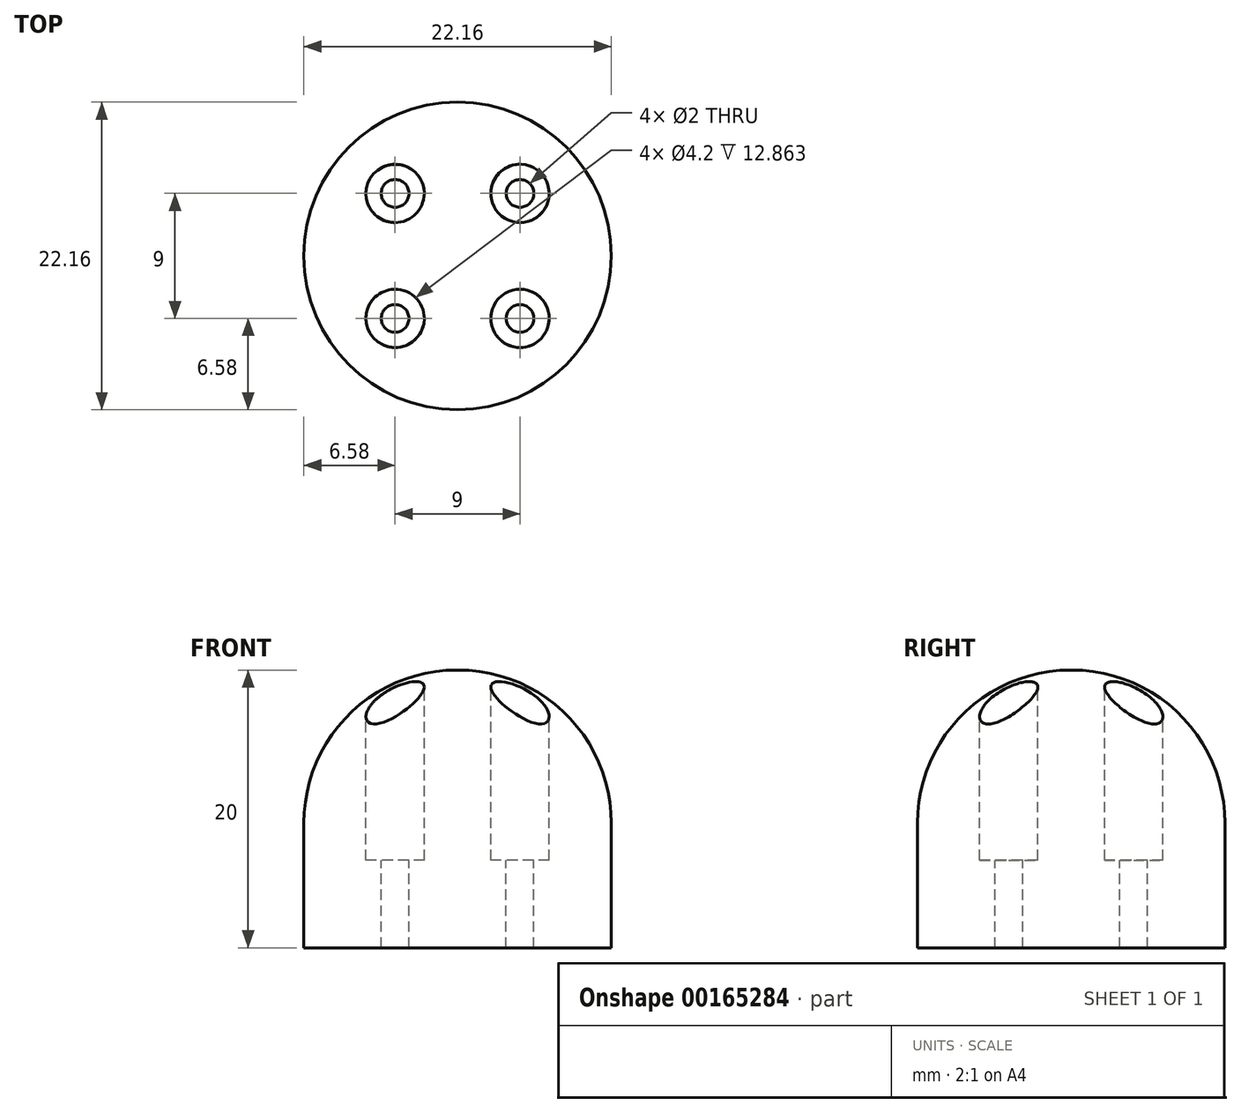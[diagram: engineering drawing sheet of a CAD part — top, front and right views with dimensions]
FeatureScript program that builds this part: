
annotation { "Feature Type Name" : "Feature", "Feature Type Description" : "" }
export const myFeature = defineFeature(function(context is Context, id is Id, definition is map)
    precondition{}
    {
        {
            var Q0;
            Q0=qCreatedBy(makeId("Top.planeOp"),FACE);
            var sketch = newSketch(context, id + "F0", { "sketchPlane" : qUnion([Q0])});
            skCircle(sketch, "E0", {"center": v(0, 0) * mm, "radius": 11.07 * mm});
            skSolve(sketch);
        }
        {
            var Q0;
            Q0=qSketchRegion(id+"F0",true);
            extrude(context, id + "F1", {"entities" : qUnion([Q0]), "depth" : 20 * mm});
        }
        {
            var Q0;
            Q0=makeQuery(id+"F1.opExtrude","CAP_FACE",FACE,{"disambiguationData":[OSD([sQuery(id+"F0.wireOp",EDGE,"E0")])],"isStart":false});
            var sketch = newSketch(context, id + "F2", { "sketchPlane" : qUnion([Q0])});
            skLineSegment(sketch, "E1.bottom", {"start": v(4.5, 4.5) * mm, "end": v(-4.5, 4.5) * mm});
            skLineSegment(sketch, "E1.top", {"start": v(4.5, -4.5) * mm, "end": v(-4.5, -4.5) * mm});
            skLineSegment(sketch, "E1.left", {"start": v(4.5, 4.5) * mm, "end": v(4.5, -4.5) * mm});
            skLineSegment(sketch, "E1.right", {"start": v(-4.5, 4.5) * mm, "end": v(-4.5, -4.5) * mm});
            skPoint(sketch, "E1.middle", {"position": v(0, 0) * mm});
            skCircle(sketch, "E2", {"center": v(-4.5, 4.5) * mm, "radius": 1 * mm, "construction": true});
            skCircle(sketch, "E3", {"center": v(4.5, 4.5) * mm, "radius": 1 * mm, "construction": true});
            skCircle(sketch, "E4", {"center": v(4.5, -4.5) * mm, "radius": 1 * mm, "construction": true});
            skCircle(sketch, "E5", {"center": v(-4.5, -4.5) * mm, "radius": 1 * mm, "construction": true});
            skCircle(sketch, "E6", {"center": v(-4.5, -4.5) * mm, "radius": 1 * mm});
            skCircle(sketch, "E7", {"center": v(-4.5, 4.5) * mm, "radius": 1 * mm});
            skCircle(sketch, "E8", {"center": v(4.5, 4.5) * mm, "radius": 1 * mm});
            skCircle(sketch, "E9", {"center": v(4.5, -4.5) * mm, "radius": 1 * mm});
            skSolve(sketch);
        }
        {
            var Q0;
            {var subQ0=sQuery(id+"F2.wireOp",EDGE,"E1.left");var subQ1=sQuery(id+"F2.wireOp",EDGE,"E1.bottom");var subQ2=makeQuery(id+"F2.imprint","INTERSECT",VERTEX,{"derivedFrom":[subQ1,subQ0]});Q0=makeQuery(id+"F2.imprint","IMPRINT",FACE,{"disambiguationData":[TD([[makeQuery(id+"F2.imprint","IMPRINT",EDGE,{"disambiguationData":[TD([[subQ2,-1.0]])],"derivedFrom":subQ1}),1.0]])]});}
            var Q1;
            {var subQ0=sQuery(id+"F2.wireOp",EDGE,"E1.right");var subQ1=sQuery(id+"F2.wireOp",EDGE,"E1.bottom");var subQ2=makeQuery(id+"F2.imprint","INTERSECT",VERTEX,{"derivedFrom":[subQ1,subQ0]});Q1=makeQuery(id+"F2.imprint","IMPRINT",FACE,{"disambiguationData":[TD([[makeQuery(id+"F2.imprint","IMPRINT",EDGE,{"disambiguationData":[TD([[subQ2,1.0]])],"derivedFrom":subQ1}),-1.0]])]});}
            var Q2;
            {var subQ0=sQuery(id+"F2.wireOp",EDGE,"E1.right");var subQ1=sQuery(id+"F2.wireOp",EDGE,"E1.bottom");var subQ2=makeQuery(id+"F2.imprint","INTERSECT",VERTEX,{"derivedFrom":[subQ1,subQ0]});Q2=makeQuery(id+"F2.imprint","IMPRINT",FACE,{"disambiguationData":[TD([[makeQuery(id+"F2.imprint","IMPRINT",EDGE,{"disambiguationData":[TD([[subQ2,1.0]])],"derivedFrom":subQ1}),1.0]])]});}
            var Q3;
            {var subQ0=sQuery(id+"F2.wireOp",EDGE,"E1.left");var subQ1=sQuery(id+"F2.wireOp",EDGE,"E1.top");var subQ2=makeQuery(id+"F2.imprint","INTERSECT",VERTEX,{"derivedFrom":[subQ1,subQ0]});Q3=makeQuery(id+"F2.imprint","IMPRINT",FACE,{"disambiguationData":[TD([[makeQuery(id+"F2.imprint","IMPRINT",EDGE,{"disambiguationData":[TD([[subQ2,-1.0]])],"derivedFrom":subQ1}),-1.0]])]});}
            var Q4;
            {var subQ0=sQuery(id+"F2.wireOp",EDGE,"E1.left");var subQ1=sQuery(id+"F2.wireOp",EDGE,"E1.top");var subQ2=makeQuery(id+"F2.imprint","INTERSECT",VERTEX,{"derivedFrom":[subQ1,subQ0]});Q4=makeQuery(id+"F2.imprint","IMPRINT",FACE,{"disambiguationData":[TD([[makeQuery(id+"F2.imprint","IMPRINT",EDGE,{"disambiguationData":[TD([[subQ2,-1.0]])],"derivedFrom":subQ1}),1.0]])]});}
            var Q5;
            {var subQ0=sQuery(id+"F2.wireOp",EDGE,"E1.right");var subQ1=sQuery(id+"F2.wireOp",EDGE,"E1.top");var subQ2=makeQuery(id+"F2.imprint","INTERSECT",VERTEX,{"derivedFrom":[subQ1,subQ0]});Q5=makeQuery(id+"F2.imprint","IMPRINT",FACE,{"disambiguationData":[TD([[makeQuery(id+"F2.imprint","IMPRINT",EDGE,{"disambiguationData":[TD([[subQ2,1.0]])],"derivedFrom":subQ1}),-1.0]])]});}
            var Q6;
            {var subQ0=sQuery(id+"F2.wireOp",EDGE,"E1.right");var subQ1=sQuery(id+"F2.wireOp",EDGE,"E1.top");var subQ2=makeQuery(id+"F2.imprint","INTERSECT",VERTEX,{"derivedFrom":[subQ1,subQ0]});Q6=makeQuery(id+"F2.imprint","IMPRINT",FACE,{"disambiguationData":[TD([[makeQuery(id+"F2.imprint","IMPRINT",EDGE,{"disambiguationData":[TD([[subQ2,1.0]])],"derivedFrom":subQ1}),1.0]])]});}
            var Q7;
            {var subQ0=sQuery(id+"F2.wireOp",EDGE,"E1.left");var subQ1=sQuery(id+"F2.wireOp",EDGE,"E1.bottom");var subQ2=makeQuery(id+"F2.imprint","INTERSECT",VERTEX,{"derivedFrom":[subQ1,subQ0]});Q7=makeQuery(id+"F2.imprint","IMPRINT",FACE,{"disambiguationData":[TD([[makeQuery(id+"F2.imprint","IMPRINT",EDGE,{"disambiguationData":[TD([[subQ2,-1.0]])],"derivedFrom":subQ1}),-1.0]])]});}
            extrude(context, id + "F3", {"entities" : qUnion([Q0, Q1, Q2, Q3, Q4, Q5, Q6, Q7]), "operationType" : NewBodyOperationType.REMOVE, "endBound" : BoundingType.THROUGH_ALL, "oppositeDirection" : true, "depth" : 25 * mm});
        }
        {
            var Q0;
            Q0=makeQuery(id+"F1.opExtrude","CAP_FACE",FACE,{"disambiguationData":[OSD([sQuery(id+"F0.wireOp",EDGE,"E0")])],"isStart":false});
            var sketch = newSketch(context, id + "F4", { "sketchPlane" : qUnion([Q0])});
            skLineSegment(sketch, "E10.bottom", {"start": v(-4.5, -4.5) * mm, "end": v(4.5, -4.5) * mm});
            skLineSegment(sketch, "E10.top", {"start": v(-4.5, 4.5) * mm, "end": v(4.5, 4.5) * mm});
            skLineSegment(sketch, "E10.left", {"start": v(-4.5, -4.5) * mm, "end": v(-4.5, 4.5) * mm});
            skLineSegment(sketch, "E10.right", {"start": v(4.5, -4.5) * mm, "end": v(4.5, 4.5) * mm});
            skPoint(sketch, "E10.middle", {"position": v(0, 0) * mm});
            skCircle(sketch, "E11", {"center": v(-4.5, 4.5) * mm, "radius": 2.1 * mm});
            skCircle(sketch, "E12", {"center": v(4.5, 4.5) * mm, "radius": 2.1 * mm});
            skCircle(sketch, "E13", {"center": v(4.5, -4.5) * mm, "radius": 2.1 * mm});
            skCircle(sketch, "E14", {"center": v(-4.5, -4.5) * mm, "radius": 2.1 * mm});
            skSolve(sketch);
        }
        {
            var Q0;
            {var subQ0=sQuery(id+"F4.wireOp",EDGE,"E14");var subQ1=sQuery(id+"F4.wireOp",EDGE,"E10.bottom");var subQ2=makeQuery(id+"F4.imprint","INTERSECT",VERTEX,{"derivedFrom":[subQ1,subQ0]});Q0=makeQuery(id+"F4.imprint","IMPRINT",FACE,{"disambiguationData":[TD([[makeQuery(id+"F4.imprint","IMPRINT",EDGE,{"disambiguationData":[TD([[subQ2,1.0]])],"derivedFrom":subQ1}),1.0]])]});}
            var Q1;
            {var subQ0=sQuery(id+"F4.wireOp",EDGE,"E14");var subQ1=sQuery(id+"F4.wireOp",EDGE,"E10.bottom");var subQ2=makeQuery(id+"F4.imprint","INTERSECT",VERTEX,{"derivedFrom":[subQ1,subQ0]});Q1=makeQuery(id+"F4.imprint","IMPRINT",FACE,{"disambiguationData":[TD([[makeQuery(id+"F4.imprint","IMPRINT",EDGE,{"disambiguationData":[TD([[subQ2,1.0]])],"derivedFrom":subQ1}),-1.0]])]});}
            var Q2;
            {var subQ0=sQuery(id+"F4.wireOp",EDGE,"E13");var subQ1=sQuery(id+"F4.wireOp",EDGE,"E10.bottom");var subQ2=makeQuery(id+"F4.imprint","INTERSECT",VERTEX,{"derivedFrom":[subQ1,subQ0]});Q2=makeQuery(id+"F4.imprint","IMPRINT",FACE,{"disambiguationData":[TD([[makeQuery(id+"F4.imprint","IMPRINT",EDGE,{"disambiguationData":[TD([[subQ2,-1.0]])],"derivedFrom":subQ1}),1.0]])]});}
            var Q3;
            {var subQ0=sQuery(id+"F4.wireOp",EDGE,"E13");var subQ1=sQuery(id+"F4.wireOp",EDGE,"E10.bottom");var subQ2=makeQuery(id+"F4.imprint","INTERSECT",VERTEX,{"derivedFrom":[subQ1,subQ0]});Q3=makeQuery(id+"F4.imprint","IMPRINT",FACE,{"disambiguationData":[TD([[makeQuery(id+"F4.imprint","IMPRINT",EDGE,{"disambiguationData":[TD([[subQ2,-1.0]])],"derivedFrom":subQ1}),-1.0]])]});}
            var Q4;
            {var subQ0=sQuery(id+"F4.wireOp",EDGE,"E11");var subQ1=sQuery(id+"F4.wireOp",EDGE,"E10.top");var subQ2=makeQuery(id+"F4.imprint","INTERSECT",VERTEX,{"derivedFrom":[subQ1,subQ0]});Q4=makeQuery(id+"F4.imprint","IMPRINT",FACE,{"disambiguationData":[TD([[makeQuery(id+"F4.imprint","IMPRINT",EDGE,{"disambiguationData":[TD([[subQ2,1.0]])],"derivedFrom":subQ1}),1.0]])]});}
            var Q5;
            {var subQ0=sQuery(id+"F4.wireOp",EDGE,"E11");var subQ1=sQuery(id+"F4.wireOp",EDGE,"E10.top");var subQ2=makeQuery(id+"F4.imprint","INTERSECT",VERTEX,{"derivedFrom":[subQ1,subQ0]});Q5=makeQuery(id+"F4.imprint","IMPRINT",FACE,{"disambiguationData":[TD([[makeQuery(id+"F4.imprint","IMPRINT",EDGE,{"disambiguationData":[TD([[subQ2,1.0]])],"derivedFrom":subQ1}),-1.0]])]});}
            var Q6;
            {var subQ0=sQuery(id+"F4.wireOp",EDGE,"E12");var subQ1=sQuery(id+"F4.wireOp",EDGE,"E10.top");var subQ2=makeQuery(id+"F4.imprint","INTERSECT",VERTEX,{"derivedFrom":[subQ1,subQ0]});Q6=makeQuery(id+"F4.imprint","IMPRINT",FACE,{"disambiguationData":[TD([[makeQuery(id+"F4.imprint","IMPRINT",EDGE,{"disambiguationData":[TD([[subQ2,-1.0]])],"derivedFrom":subQ1}),-1.0]])]});}
            var Q7;
            {var subQ0=sQuery(id+"F4.wireOp",EDGE,"E12");var subQ1=sQuery(id+"F4.wireOp",EDGE,"E10.top");var subQ2=makeQuery(id+"F4.imprint","INTERSECT",VERTEX,{"derivedFrom":[subQ1,subQ0]});Q7=makeQuery(id+"F4.imprint","IMPRINT",FACE,{"disambiguationData":[TD([[makeQuery(id+"F4.imprint","IMPRINT",EDGE,{"disambiguationData":[TD([[subQ2,-1.0]])],"derivedFrom":subQ1}),1.0]])]});}
            var Q8;
            {var subQ0=sQuery(id+"F4.wireOp",EDGE,"E10.left");var subQ1=sQuery(id+"F4.wireOp",EDGE,"E10.bottom");var subQ2=makeQuery(id+"F4.imprint","INTERSECT",VERTEX,{"derivedFrom":[subQ1,subQ0]});Q8=makeQuery(id+"F4.imprint","IMPRINT",FACE,{"disambiguationData":[TD([[makeQuery(id+"F4.imprint","IMPRINT",EDGE,{"disambiguationData":[TD([[subQ2,-1.0]])],"derivedFrom":subQ1}),1.0]])]});}
            var Q9;
            {var subQ0=sQuery(id+"F4.wireOp",EDGE,"E10.left");var subQ1=sQuery(id+"F4.wireOp",EDGE,"E10.bottom");var subQ2=makeQuery(id+"F4.imprint","INTERSECT",VERTEX,{"derivedFrom":[subQ1,subQ0]});Q9=makeQuery(id+"F4.imprint","IMPRINT",FACE,{"disambiguationData":[TD([[makeQuery(id+"F4.imprint","IMPRINT",EDGE,{"disambiguationData":[TD([[subQ2,-1.0]])],"derivedFrom":subQ1}),-1.0]])]});}
            var Q10;
            {var subQ0=sQuery(id+"F4.wireOp",EDGE,"E10.right");var subQ1=sQuery(id+"F4.wireOp",EDGE,"E10.bottom");var subQ2=makeQuery(id+"F4.imprint","INTERSECT",VERTEX,{"derivedFrom":[subQ1,subQ0]});Q10=makeQuery(id+"F4.imprint","IMPRINT",FACE,{"disambiguationData":[TD([[makeQuery(id+"F4.imprint","IMPRINT",EDGE,{"disambiguationData":[TD([[subQ2,1.0]])],"derivedFrom":subQ1}),1.0]])]});}
            var Q11;
            {var subQ0=sQuery(id+"F4.wireOp",EDGE,"E10.right");var subQ1=sQuery(id+"F4.wireOp",EDGE,"E10.bottom");var subQ2=makeQuery(id+"F4.imprint","INTERSECT",VERTEX,{"derivedFrom":[subQ1,subQ0]});Q11=makeQuery(id+"F4.imprint","IMPRINT",FACE,{"disambiguationData":[TD([[makeQuery(id+"F4.imprint","IMPRINT",EDGE,{"disambiguationData":[TD([[subQ2,1.0]])],"derivedFrom":subQ1}),-1.0]])]});}
            var Q12;
            {var subQ0=sQuery(id+"F4.wireOp",EDGE,"E10.left");var subQ1=sQuery(id+"F4.wireOp",EDGE,"E10.top");var subQ2=makeQuery(id+"F4.imprint","INTERSECT",VERTEX,{"derivedFrom":[subQ1,subQ0]});Q12=makeQuery(id+"F4.imprint","IMPRINT",FACE,{"disambiguationData":[TD([[makeQuery(id+"F4.imprint","IMPRINT",EDGE,{"disambiguationData":[TD([[subQ2,-1.0]])],"derivedFrom":subQ1}),1.0]])]});}
            var Q13;
            {var subQ0=sQuery(id+"F4.wireOp",EDGE,"E10.left");var subQ1=sQuery(id+"F4.wireOp",EDGE,"E10.top");var subQ2=makeQuery(id+"F4.imprint","INTERSECT",VERTEX,{"derivedFrom":[subQ1,subQ0]});Q13=makeQuery(id+"F4.imprint","IMPRINT",FACE,{"disambiguationData":[TD([[makeQuery(id+"F4.imprint","IMPRINT",EDGE,{"disambiguationData":[TD([[subQ2,-1.0]])],"derivedFrom":subQ1}),-1.0]])]});}
            var Q14;
            {var subQ0=sQuery(id+"F4.wireOp",EDGE,"E10.right");var subQ1=sQuery(id+"F4.wireOp",EDGE,"E10.top");var subQ2=makeQuery(id+"F4.imprint","INTERSECT",VERTEX,{"derivedFrom":[subQ1,subQ0]});Q14=makeQuery(id+"F4.imprint","IMPRINT",FACE,{"disambiguationData":[TD([[makeQuery(id+"F4.imprint","IMPRINT",EDGE,{"disambiguationData":[TD([[subQ2,1.0]])],"derivedFrom":subQ1}),-1.0]])]});}
            var Q15;
            {var subQ0=sQuery(id+"F4.wireOp",EDGE,"E10.right");var subQ1=sQuery(id+"F4.wireOp",EDGE,"E10.top");var subQ2=makeQuery(id+"F4.imprint","INTERSECT",VERTEX,{"derivedFrom":[subQ1,subQ0]});Q15=makeQuery(id+"F4.imprint","IMPRINT",FACE,{"disambiguationData":[TD([[makeQuery(id+"F4.imprint","IMPRINT",EDGE,{"disambiguationData":[TD([[subQ2,1.0]])],"derivedFrom":subQ1}),1.0]])]});}
            extrude(context, id + "F5", {"entities" : qUnion([Q0, Q1, Q2, Q3, Q4, Q5, Q6, Q7, Q8, Q9, Q10, Q11, Q12, Q13, Q14, Q15]), "operationType" : NewBodyOperationType.REMOVE, "oppositeDirection" : true, "depth" : 13.7 * mm});
        }
        {
            var Q0;
            Q0=makeQuery(id+"F1.opExtrude","CAP_EDGE",EDGE,{"disambiguationData":[OSD([sQuery(id+"F0.wireOp",EDGE,"E0")])],"isStart":false});
            fillet(context, id + "F6", {"entities" : qUnion([Q0]), "radius" : 11 * mm, "tangentPropagation" : true, "allowEdgeOverflow" : false});
        }
    });
